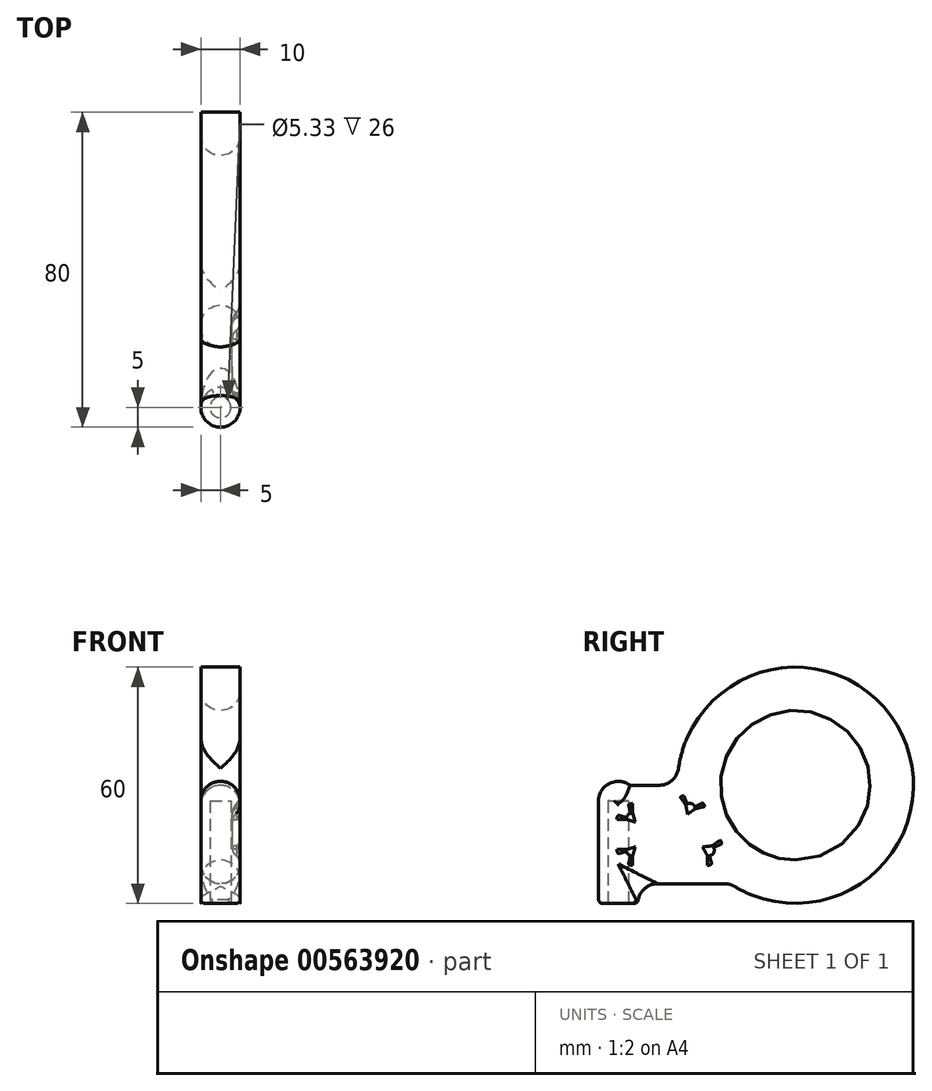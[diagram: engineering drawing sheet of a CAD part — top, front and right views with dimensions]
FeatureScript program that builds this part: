
annotation { "Feature Type Name" : "Feature", "Feature Type Description" : "" }
export const myFeature = defineFeature(function(context is Context, id is Id, definition is map)
    precondition{}
    {
        {
            var Q0;
            Q0=qCreatedBy(makeId("Top.planeOp"),FACE);
            var sketch = newSketch(context, id + "F0", { "sketchPlane" : qUnion([Q0])});
            skCircle(sketch, "E0", {"center": v(0, 0) * mm, "radius": 2.6 * mm});
            skCircle(sketch, "E1", {"center": v(0, 0) * mm, "radius": 5 * mm});
            skSolve(sketch);
        }
        {
            var Q0;
            Q0=makeQuery(id+"F0.imprint","IMPRINT",FACE,{"disambiguationData":[TD([[makeQuery(id+"F0.imprint","IMPRINT",EDGE,{"derivedFrom":sQuery(id+"F0.wireOp",EDGE,"E0")}),-1.0]])]});
            extrude(context, id + "F1", {"entities" : qUnion([Q0]), "depth" : 26 * mm, "offsetDistance" : 25 * mm});
        }
        {
            var Q0;
            Q0=makeQuery(id+"F1.opExtrude","CAP_FACE",FACE,{"disambiguationData":[OSD([sQuery(id+"F0.wireOp",EDGE,"E0"),sQuery(id+"F0.wireOp",EDGE,"E1")])],"isStart":false});
            var sketch = newSketch(context, id + "F2", { "sketchPlane" : qUnion([Q0])});
            skCircle(sketch, "E2", {"center": v(0, 0) * mm, "radius": 5 * mm});
            skSolve(sketch);
        }
        {
            var Q0;
            Q0 = qSketchRegion(id + "F2", true);
            extrude(context, id + "F3", {"entities" : qUnion([Q0]), "operationType" : NewBodyOperationType.ADD, "depth" : 5 * mm, "offsetDistance" : 25 * mm});
        }
        {
            var Q0;
            Q0=makeQuery(id+"F3.opExtrude","CAP_EDGE",EDGE,{"disambiguationData":[OSD([sQuery(id+"F2.wireOp",EDGE,"E2")])],"isStart":false});
            fillet(context, id + "F4", {"entities" : qUnion([Q0]), "radius" : 5 * mm, "tangentPropagation" : true, "allowEdgeOverflow" : false});
        }
        {
            var Q0;
            Q0=qCreatedBy(makeId("Right.planeOp"),FACE);
            var sketch = newSketch(context, id + "F5", { "sketchPlane" : qUnion([Q0])});
            skArc(sketch, "E3", {"start": v(28.42, 5) * mm, "mid": v(71.43, 44.19) * mm, "end": v(15, 30) * mm});
            skCircle(sketch, "E4", {"center": v(45, 30) * mm, "radius": 19 * mm});
            skLineSegment(sketch, "E5.top", {"start": v(28.42, 5) * mm, "end": v(0, 5) * mm});
            skLineSegment(sketch, "E5.right", {"start": v(0, 30) * mm, "end": v(0, 5) * mm});
            skLineSegment(sketch, "E6.trimOffspring", {"start": v(15, 30) * mm, "end": v(0, 30) * mm});
            skSolve(sketch);
        }
        {
            var Q0;
            Q0 = qSketchRegion(id + "F5", true);
            extrude(context, id + "F6", {"entities" : qUnion([Q0]), "operationType" : NewBodyOperationType.ADD, "depth" : 5 * mm, "offsetDistance" : 25 * mm});
        }
        {
            var Q0;
            Q0 = qSketchRegion(id + "F5", true);
            extrude(context, id + "F7", {"entities" : qUnion([Q0]), "operationType" : NewBodyOperationType.ADD, "depth" : -5 * mm, "offsetDistance" : 25 * mm});
        }
        {
            var Q0;
            Q0=makeQuery(id+"F6.opExtrude","CAP_EDGE",EDGE,{"disambiguationData":[OSD([sQuery(id+"F5.wireOp",EDGE,"E6.trimOffspring")])],"isStart":false});
            var Q1;
            Q1=makeQuery(id+"F7.opExtrude","CAP_EDGE",EDGE,{"disambiguationData":[OSD([sQuery(id+"F5.wireOp",EDGE,"E6.trimOffspring")])],"isStart":false});
            var Q2;
            {var subQ0=sQuery(id+"F5.wireOp",EDGE,"E6.trimOffspring");var subQ1=sQuery(id+"F5.wireOp",EDGE,"E3");Q2=makeQuery(id+"F7.boolean.opBoolean","MERGE",EDGE,{"derivedFrom":[makeQuery(id+"F6.opExtrude","SWEPT_EDGE",EDGE,{"disambiguationData":[OSD([subQ1,subQ0])]}),makeQuery(id+"F7.opExtrude","SWEPT_EDGE",EDGE,{"disambiguationData":[OSD([subQ1,subQ0])]})]});}
            var Q3;
            {var subQ0=sQuery(id+"F5.wireOp",EDGE,"E5.top");Q3=makeQuery(id+"F7.boolean.opBoolean","MERGE",FACE,{"derivedFrom":[makeQuery(id+"F6.boolean.opBoolean","SPLIT",FACE,{"disambiguationData":[TD([makeQuery(id+"F1.opExtrude","SWEPT_FACE",FACE,{"disambiguationData":[OSD([sQuery(id+"F0.wireOp",EDGE,"E1")])]})])],"derivedFrom":makeQuery(id+"F6.opExtrude","SWEPT_FACE",FACE,{"disambiguationData":[OSD([subQ0])]})}),makeQuery(id+"F7.opExtrude","SWEPT_FACE",FACE,{"disambiguationData":[OSD([subQ0])]})]});}
            var Q4;
            {var subQ0=sQuery(id+"F5.wireOp",EDGE,"E4");Q4=makeQuery(id+"F7.boolean.opBoolean","MERGE",FACE,{"derivedFrom":[makeQuery(id+"F6.opExtrude","SWEPT_FACE",FACE,{"disambiguationData":[OSD([subQ0])]}),makeQuery(id+"F7.opExtrude","SWEPT_FACE",FACE,{"disambiguationData":[OSD([subQ0])]})]});}
            var Q5;
            Q5=makeQuery(id+"F6.opExtrude","CAP_EDGE",EDGE,{"disambiguationData":[OSD([sQuery(id+"F5.wireOp",EDGE,"E4")])],"isStart":false});
            fillet(context, id + "F8", {"entities" : qUnion([Q0, Q1, Q2, Q3, Q4, Q5]), "radius" : 5 * mm, "tangentPropagation" : true, "allowEdgeOverflow" : false});
        }
        {
            var Q0;
            Q0=makeQuery(id+"F1.opExtrude","CAP_EDGE",EDGE,{"disambiguationData":[OSD([sQuery(id+"F0.wireOp",EDGE,"E1")])],"isStart":true});
            fillet(context, id + "F9", {"entities" : qUnion([Q0]), "radius" : 1 * mm, "tangentPropagation" : true, "allowEdgeOverflow" : false});
        }
        {
            var Q0;
            Q0=makeQuery(id+"F1.opExtrude","CAP_FACE",FACE,{"disambiguationData":[OSD([sQuery(id+"F0.wireOp",EDGE,"E0"),sQuery(id+"F0.wireOp",EDGE,"E1")])],"isStart":true});
            var sketch = newSketch(context, id + "F10", { "sketchPlane" : qUnion([Q0])});
            skCircle(sketch, "E7", {"center": v(0, 0) * mm, "radius": 2.67 * mm});
            skSolve(sketch);
        }
        {
            var Q0;
            Q0 = qSketchRegion(id + "F10", true);
            extrude(context, id + "F11", {"entities" : qUnion([Q0]), "operationType" : NewBodyOperationType.REMOVE, "oppositeDirection" : true, "depth" : 26 * mm, "offsetDistance" : 25 * mm});
        }
        {
            var Q0;
            Q0=makeQuery(id+"F6.opExtrude","CAP_FACE",FACE,{"disambiguationData":[OSD([sQuery(id+"F5.wireOp",EDGE,"E3"),sQuery(id+"F5.wireOp",EDGE,"E4"),sQuery(id+"F5.wireOp",EDGE,"E5.top"),sQuery(id+"F5.wireOp",EDGE,"E5.right"),sQuery(id+"F5.wireOp",EDGE,"E6.trimOffspring")])],"isStart":false});
            var sketch = newSketch(context, id + "F12", { "sketchPlane" : qUnion([Q0])});
            skArc(sketch, "E8.0", {"start": v(27.46, 11.49) * mm, "mid": v(27.22, 11.5) * mm, "end": v(26.97, 11.5) * mm});
            skArc(sketch, "E8.1", {"start": v(10.36, 23.5) * mm, "mid": v(13.85, 24.04) * mm, "end": v(17, 25.62) * mm});
            skLineSegment(sketch, "E8.2", {"start": v(10.36, 23.5) * mm, "end": v(3.5, 23.5) * mm});
            skLineSegment(sketch, "E8.3", {"start": v(1.5, 21.5) * mm, "end": v(1.5, 13.5) * mm});
            skLineSegment(sketch, "E8.4", {"start": v(3.5, 11.5) * mm, "end": v(23, 11.5) * mm});
            skArc(sketch, "E9.0", {"start": v(24.6, 14.7) * mm, "mid": v(21.84, 19.32) * mm, "end": v(20.12, 24.42) * mm});
            skPoint(sketch, "E10.visualSharp", {"position": v(19.57, 28.11) * mm});
            skArc(sketch, "E10.filletArc", {"start": v(20.12, 24.42) * mm, "mid": v(18.88, 25.85) * mm, "end": v(17, 25.62) * mm});
            skArc(sketch, "E11.filletArc", {"start": v(23, 11.5) * mm, "mid": v(24.79, 12.6) * mm, "end": v(24.6, 14.7) * mm});
            skPoint(sketch, "E12.visualSharp", {"position": v(1.5, 23.5) * mm});
            skArc(sketch, "E12.filletArc", {"start": v(3.5, 23.5) * mm, "mid": v(2.09, 22.91) * mm, "end": v(1.5, 21.5) * mm});
            skPoint(sketch, "E13.visualSharp", {"position": v(1.5, 11.5) * mm});
            skArc(sketch, "E13.filletArc", {"start": v(1.5, 13.5) * mm, "mid": v(2.09, 12.09) * mm, "end": v(3.5, 11.5) * mm});
            skSolve(sketch);
        }
        {
            var Q0;
            Q0 = qSketchRegion(id + "F12", true);
            extrude(context, id + "F13", {"entities" : qUnion([Q0]), "operationType" : NewBodyOperationType.REMOVE, "oppositeDirection" : true, "depth" : 2 * mm, "offsetDistance" : 25 * mm});
        }
        {
            var Q0;
            Q0=makeQuery(id+"F13.boolean.opBoolean","COPY",EDGE,{"derivedFrom":makeQuery(id+"F13.opExtrude","CAP_EDGE",EDGE,{"disambiguationData":[OSD([sQuery(id+"F12.wireOp",EDGE,"E8.3")])],"isStart":false})});
            fillet(context, id + "F14", {"entities" : qUnion([Q0]), "radius" : 3 * mm, "tangentPropagation" : true, "allowEdgeOverflow" : false});
        }
        {
            var Q0;
            Q0=makeQuery(id+"F14.opFillet","BLEND_EDGE",EDGE,{"blendedFrom":[makeQuery(id+"F13.boolean.opBoolean","COPY",EDGE,{"derivedFrom":makeQuery(id+"F13.opExtrude","CAP_EDGE",EDGE,{"disambiguationData":[OSD([sQuery(id+"F12.wireOp",EDGE,"E8.2")])],"isStart":false})}),makeQuery(id+"F6.opExtrude","CAP_FACE",FACE,{"disambiguationData":[OSD([sQuery(id+"F5.wireOp",EDGE,"E3"),sQuery(id+"F5.wireOp",EDGE,"E4"),sQuery(id+"F5.wireOp",EDGE,"E5.top"),sQuery(id+"F5.wireOp",EDGE,"E5.right"),sQuery(id+"F5.wireOp",EDGE,"E6.trimOffspring")])],"isStart":false})],"blendedInto":[makeQuery(id+"F6.opExtrude","CAP_FACE",FACE,{"disambiguationData":[OSD([sQuery(id+"F5.wireOp",EDGE,"E3"),sQuery(id+"F5.wireOp",EDGE,"E4"),sQuery(id+"F5.wireOp",EDGE,"E5.top"),sQuery(id+"F5.wireOp",EDGE,"E5.right"),sQuery(id+"F5.wireOp",EDGE,"E6.trimOffspring")])],"isStart":false})]});
            fillet(context, id + "F15", {"entities" : qUnion([Q0]), "radius" : 3 * mm, "tangentPropagation" : true, "allowEdgeOverflow" : false});
        }
    });
